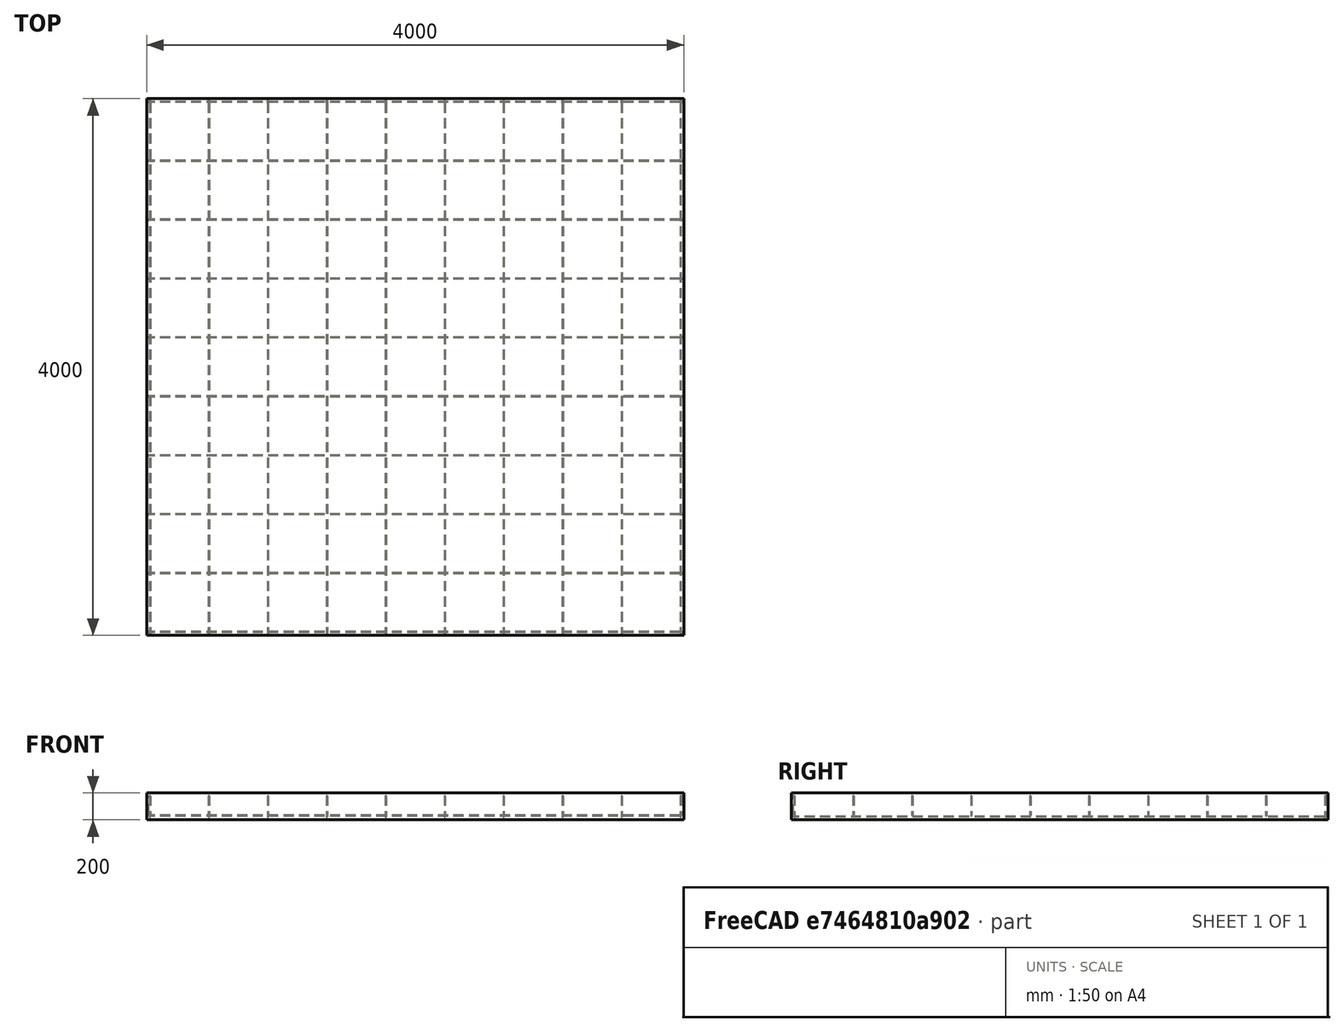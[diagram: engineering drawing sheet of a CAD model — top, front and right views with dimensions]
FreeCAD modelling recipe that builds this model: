
FCSTD DOCUMENT  (FreeCAD 0.20R29177 (Git))
Label: slab
License: All rights reserved
objects: Part::FeaturePython×3, Sketcher::SketchObject×2, Part::Part2DObjectPython×1, App::DocumentObjectGroupPython×1
note: 6 computed .brp shape members not serialized (recipe doc carries the construction recipe); baked Part::Feature solids carry a one-line shape summary decoded from their .brp

FEATURE [Part::Part2DObjectPython] Rectangle  # Draft 2D object (typed FeaturePython)
  Area = 1.6e+07
  ChamferSize = 0
  Columns = 1
  FilletRadius = 0
  Height = 4000
  Length = 4000
  MakeFace = true
  Rows = 1
FEATURE [Part::FeaturePython] Structure  label="Slab"  # Arch/BIM 118 (typed FeaturePython)
  Base = -> Rectangle
  BaseMirror = false
  BaseOffsetX = 0
  BaseOffsetY = 0
  BasePerpendicularToTool = false
  BaseRotation = 0
  ComputedLength = 200
  FaceMaker = 0
  Height = 200
  HorizontalArea = 1.6e+07
  IfcData = attributes={"GlobalId": {"name": "GlobalId", "type": "IfcGloballyUniqueId", "is_enum": false, "enum_values": []}, "Description": {"... (+453 chars omitted),+1 more (map truncated)
  IfcType = 118
  Length = 4000
  MoveBase = false
  MoveWithHost = false
  Nodes = (4) [(0,0,0),(4000,0,0),(4000,4000,0),(0,4000,0)]
  NodesOffset = 0
  Normal = (0,0,-1)
  PerimeterLength = 16000
  PredefinedType = 0
  ToolOffsetFirst = 0
  ToolOffsetLast = 0
  VerticalArea = 3.2e+06
  Width = 4000
FEATURE [Sketcher::SketchObject] Sketch
  FullyConstrained = false
  MapMode = 5
  Placement = pos=(0,0,0) rot=(0.57735,-0.57735,-0.57735;2.0944rad)
  Support = -> [Structure]
  sketch-geometry (3):
    g0: LineSegment StartX=-3986 StartY=-20 StartZ=0 EndX=-3986 EndY=-176 EndZ=0
    g1: LineSegment StartX=-3986 StartY=-176 StartZ=0 EndX=-14 EndY=-176 EndZ=0
    g2: LineSegment StartX=-14 StartY=-176 StartZ=0 EndX=-14 EndY=-20 EndZ=0
FEATURE [Part::FeaturePython] Rebar  label="UShapeRebar"  # Arch/BIM 110 (typed FeaturePython)
  Amount = 10
  AmountCheck = true
  Base = -> Sketch
  BottomCover = 20
  Diameter = 8
  Direction = (0,0,0)
  Distance = 0
  FrontCover = 20
  HorizontalArea = 0
  Host = -> Structure
  IfcType = 110
  LeftCover = 10
  Length = 4284
  Mark = UShapeRebar
  MoveBase = false
  MoveWithHost = false
  OffsetEnd = 24
  OffsetStart = 24
  Orientation = Bottom
  PerimeterLength = 0
  PlacementList = 10 placements: arithmetic series from (24,0,0) step (439.111,0,0) to (3976,0,0)
  RebarShape = 1
  RightCover = 10
  Rounding = 2
  Spacing = 439.111
  TopCover = 20
  TotalLength = 42840
  TrueSpacing = 10
  VerticalArea = 0
FEATURE [Sketcher::SketchObject] Sketch001
  FullyConstrained = false
  MapMode = 5
  Placement = pos=(0,4000,0) rot=(0,0.707107,0.707107;3.14159rad)
  Support = -> [Structure]
  sketch-geometry (3):
    g0: LineSegment StartX=-3986 StartY=-20 StartZ=0 EndX=-3986 EndY=-168 EndZ=0
    g1: LineSegment StartX=-3986 StartY=-168 StartZ=0 EndX=-14 EndY=-168 EndZ=0
    g2: LineSegment StartX=-14 StartY=-168 StartZ=0 EndX=-14 EndY=-20 EndZ=0
FEATURE [Part::FeaturePython] Rebar001  label="UShapeRebar001"  # Arch/BIM 110 (typed FeaturePython)
  Amount = 10
  AmountCheck = true
  Base = -> Sketch001
  BottomCover = 28
  Diameter = 8
  Direction = (0,0,0)
  Distance = 0
  FrontCover = 20
  HorizontalArea = 0
  Host = -> Structure
  IfcType = 110
  LeftCover = 10
  Length = 4268
  Mark = UShapeRebar001
  MoveBase = false
  MoveWithHost = false
  OffsetEnd = 24
  OffsetStart = 24
  Orientation = Bottom
  PerimeterLength = 0
  PlacementList = 10 placements: arithmetic series from (0,-24,5.32907e-15) step (0,-439.111,9.75023e-14) to (0,-3976,8.82849e-13)
  RebarShape = 1
  RightCover = 10
  Rounding = 2
  Spacing = 439.111
  TopCover = 20
  TotalLength = 42680
  TrueSpacing = 10
  VerticalArea = 0
FEATURE [App::DocumentObjectGroupPython] SlabReinforcement  # scripted group (container) (typed FeaturePython)
  CrossAmountSpacingCheck = true
  CrossAmountValue = 10
  CrossBentBarAngle = 135
  CrossBentBarLength = 50
  CrossBottomCover = 20
  CrossDiameter = 8
  CrossDistributionRebarsAmount = 3
  CrossDistributionRebarsAmountSpacingCheck = true
  CrossDistributionRebarsCheck = false
  CrossDistributionRebarsDiameter = 8
  CrossDistributionRebarsSpacing = 20
  CrossFrontCover = 20
  CrossLShapeHookOrintation = 0
  CrossLeftCover = 10
  CrossRearCover = 20
  CrossRebarType = 2
  CrossRebars = -> [Rebar001]
  CrossRightCover = 10
  CrossRounding = 2
  CrossSpacingValue = 50
  CrossTopCover = 20
  Facename = Face4
  Group = -> [Rebar,Rebar001]
  IsMakeOrEditRequired = true
  MeshCoverAlong = 0
  ParallelAmountSpacingCheck = true
  ParallelAmountValue = 10
  ParallelBentBarAngle = 135
  ParallelBentBarLength = 50
  ParallelBottomCover = 20
  ParallelDiameter = 8
  ParallelDistributionRebarsAmount = 3
  ParallelDistributionRebarsAmountSpacingCheck = true
  ParallelDistributionRebarsCheck = false
  ParallelDistributionRebarsDiameter = 8
  ParallelDistributionRebarsSpacing = 20
  ParallelFrontCover = 20
  ParallelLShapeHookOrintation = 0
  ParallelLeftCover = 10
  ParallelRearCover = 20
  ParallelRebarType = 2
  ParallelRebars = -> [Rebar]
  ParallelRightCover = 10
  ParallelRounding = 2
  ParallelSpacingValue = 50
  ParallelTopCover = 20
  Structure = -> Structure
